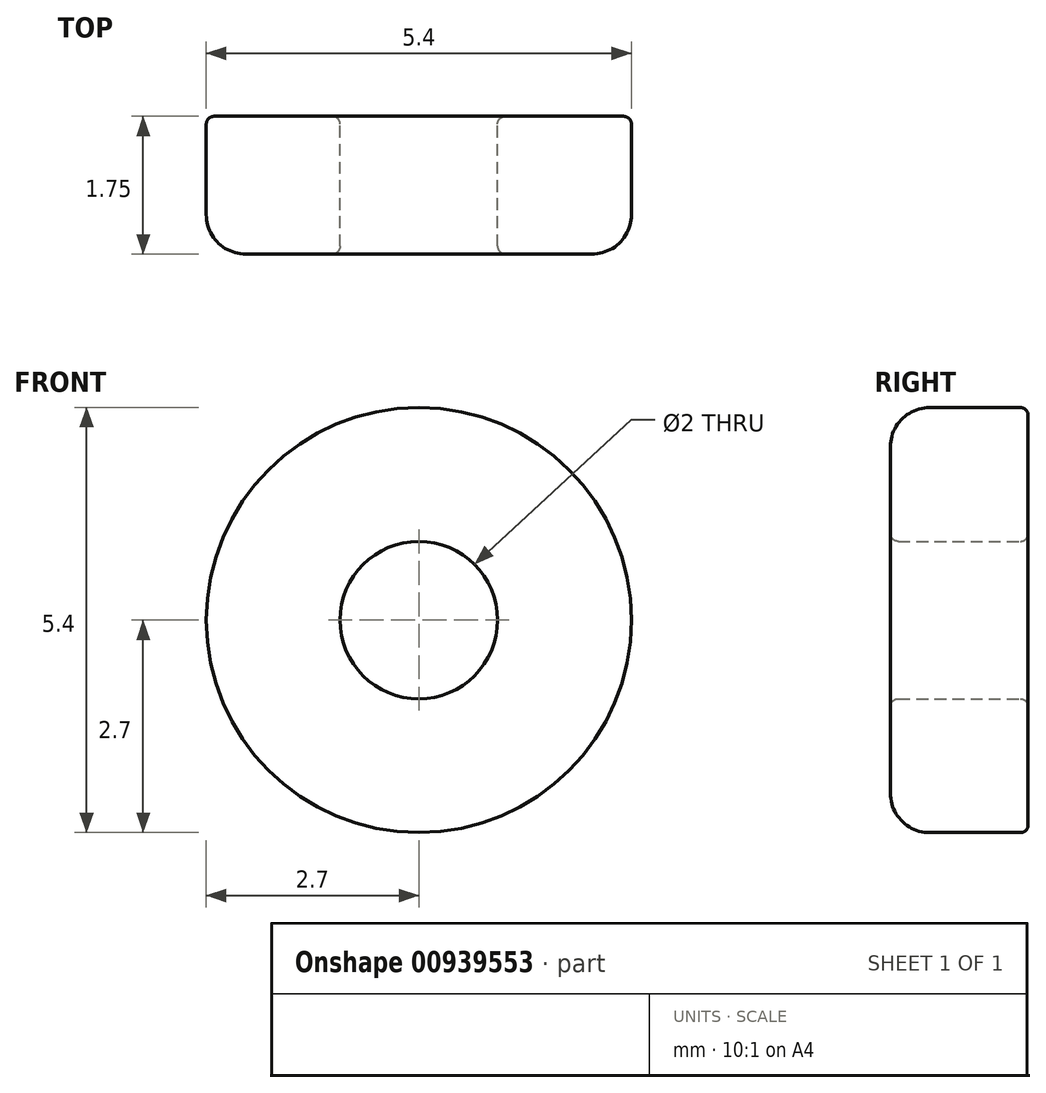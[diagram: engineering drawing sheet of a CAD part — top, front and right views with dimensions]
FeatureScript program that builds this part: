
annotation { "Feature Type Name" : "Feature", "Feature Type Description" : "" }
export const myFeature = defineFeature(function(context is Context, id is Id, definition is map)
    precondition{}
    {
        {
            var Q0;
            Q0=qCreatedBy(makeId("Front.planeOp"),FACE);
            var sketch = newSketch(context, id + "F0", { "sketchPlane" : qUnion([Q0])});
            skCircle(sketch, "E0", {"center": v(0, 0) * mm, "radius": 1 * mm});
            skCircle(sketch, "E1", {"center": v(0, 0) * mm, "radius": 2.7 * mm});
            skSolve(sketch);
        }
        {
            var Q0;
            Q0=makeQuery(id+"F0.imprint","IMPRINT",FACE,{"disambiguationData":[TD([[makeQuery(id+"F0.imprint","IMPRINT",EDGE,{"derivedFrom":sQuery(id+"F0.wireOp",EDGE,"E0")}),-1.0]])]});
            extrude(context, id + "F1", {"entities" : qUnion([Q0]), "depth" : 1.75 * mm, "offsetDistance" : 25 * mm});
        }
        {
            var Q0;
            Q0=makeQuery(id+"F1.opExtrude","CAP_EDGE",EDGE,{"disambiguationData":[OSD([sQuery(id+"F0.wireOp",EDGE,"E1")])],"isStart":false});
            fillet(context, id + "F2", {"entities" : qUnion([Q0]), "radius" : .5 * mm, "tangentPropagation" : true, "allowEdgeOverflow" : false});
        }
        {
            var Q0;
            Q0=makeQuery(id+"F1.opExtrude","CAP_EDGE",EDGE,{"disambiguationData":[OSD([sQuery(id+"F0.wireOp",EDGE,"E0")])],"isStart":false});
            var Q1;
            Q1=makeQuery(id+"F1.opExtrude","CAP_EDGE",EDGE,{"disambiguationData":[OSD([sQuery(id+"F0.wireOp",EDGE,"E1")])],"isStart":true});
            var Q2;
            Q2=makeQuery(id+"F1.opExtrude","CAP_EDGE",EDGE,{"disambiguationData":[OSD([sQuery(id+"F0.wireOp",EDGE,"E0")])],"isStart":true});
            fillet(context, id + "F3", {"entities" : qUnion([Q0, Q1, Q2]), "radius" : .1 * mm, "tangentPropagation" : true, "allowEdgeOverflow" : false});
        }
    });
